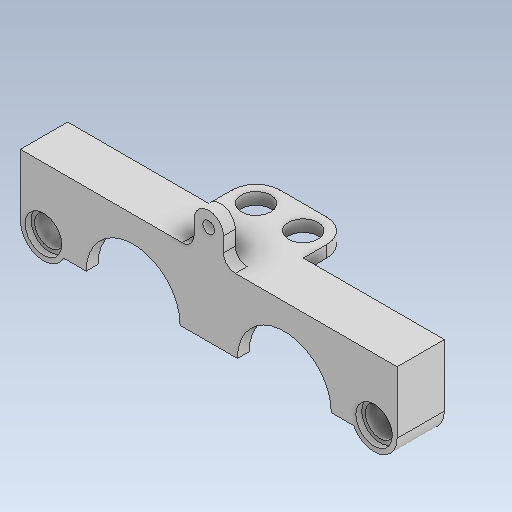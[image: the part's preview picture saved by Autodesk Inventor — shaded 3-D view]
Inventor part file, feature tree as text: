
AUTODESK INVENTOR PART (.ipt)
format: ipt  version: 2020 (Build 240168000, 168)  size: 237,568 bytes
history: native  units: mm
features: other x23, extrude x9, sketch x9
ambient origin geometry x8: Origin, YZ Plane, XZ Plane, XY Plane, X Axis, Y Axis, Z Axis, Center Point
bodies: Body1 (feature_tree)
feature tree (41):
  other  "Sólido1"
  extrude  "Extrusão1"  Depth=2.0mm
  extrude  "Extrusão2"  Depth=2.0mm TaperAngle=0.0deg
  extrude  "Extrusão3"  Depth=6.2mm
  extrude  "Extrusão4"  Depth=1.0mm
  extrude  "Extrusão5"  Depth=2.0mm TaperAngle=0.0deg
  extrude  "Extrusão6"  Depth=2.0mm
  extrude  "Extrusão7"  Depth=2.0mm
  extrude  "Extrusão8"  Depth=8.0mm TaperAngle=0.0deg
  extrude  "Extrusão9"  Depth=5.0mm
  sketch  "Esboço1"  dims[d0=7.8mm d1=2.0mm]
  other  "Referência1"
  other  "Referência2"
  other  "Referência3"
  other  "Referência4"
  other  "Referência5"
  other  "Referência6"
  sketch  "Esboço3"  dims[d2=8.0mm d3=0.0mm d4=2.0mm d5=0.0mm]
  other  "Referência7"
  other  "Referência8"
  sketch  "Esboço4"  dims[d6=6.2mm d7=6.2mm]
  sketch  "Esboço5"  dims[d8=1.0mm d9=0.0mm d10=6.2mm]
  other  "Referência9"
  other  "Referência10"
  other  "Referência11"
  sketch  "Esboço6"  dims[d11=1.0mm d12=0.0mm d15=2.0mm d16=0.0mm]
  other  "Referência13"
  sketch  "Esboço8"  dims[d19=29.4mm d20=2.0mm]
  other  "Referência16"
  sketch  "Esboço9"  dims[d22=2.0mm d23=2.0mm]
  other  "Referência17"
  other  "Referência18"
  sketch  "Esboço10"  dims[d24=16.0mm d25=8.0mm d26=0.0mm]
  sketch  "Esboço11"  dims[d27=6.75mm d28=0.0mm d29=5.0mm d30=5.0mm d31=15.25mm d32=0.0mm d33=5.0mm d34=5.0mm d35=10.0mm d36=0.0mm]
  other  "<userpath>\Desktop\rabo\3d\ela.iam"
  other  "ela.iam"
  other  "basesinha:1"
  other  "Component2_3_MIR:1"
  other  "Component2_3:1"
  other  "ultrassonicohc-sr04:1"
  other  "Component2_6:2"
